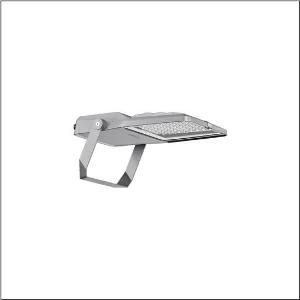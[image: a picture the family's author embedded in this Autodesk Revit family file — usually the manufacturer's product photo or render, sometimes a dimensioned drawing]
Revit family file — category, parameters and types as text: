
# Revit family: floodlight_fl_21_mini___pl61_5xa7776c2c1a_8570
name_source: partatom
category: Lighting Fixtures
units: mm (PartAtom-declared; Revit-internal decimal feet)

## family parameters
Cut with Voids When Loaded = No
Host = Face
Light Source = No
Part Type = Normal
Room Calculation Point = No
Round Connector Dimension = Use Diameter
Shared = No

## types (1)
- --- (1 x LED, 11960 lm, 89 W, 3000K)
    Apparent Load = 89 VA
    CIE Flux Codes = 33 65 98 100 100
    Color Rendering = 70
    Color Temperature = 3000K
    Default Elevation = 1800 mm
    Description = Floodlight FL 21 mini, floodlight, primary light control with lens, of PMMA, primary optical cover: protective disc, of toughened safety glass, transparent, light distribution: PL61, light emission: direct distribution, installation type: surface-mounted, LED, High Power LED, rated luminous flux: 11.960lm, luminous efficacy: 134lm/W, light colour: 730, colour temperature: 3000K, control gear: Smart Interface (Zhaga), control: flexible luminous flux parameterisation, time-dependent luminous flux control, constant luminous flux control, overheat protection, pre-setting: logarithmic dimming characteristic, with terminal, 6-pole, mains connection: 220..240V, AC, 50/60Hz, start of lifetime: 89W, end of service life: 94W, reduction: 43W, luminaire housing, of diecast aluminium, powder-coated, SITECO metallic grey (DB 702S), corrosivity category C5 mid according to DIN EN ISO 12944, suitable for swimming pools, chlorine-resistant, sealing non-destructively replaceable, mounting bracket, of steel, galvanised, powder-coated, SITECO metallic grey (DB 702S), Smart Interface below and above, protection rating (complete): IP66, insulation class (complete): insulation class II (safety insulation), certification: CE, ENEC, VDE, protection symbol: D, impact resistance: IK08, permissible operating ambient temperature: -40..+40°C, permissible operating ambient temperature for outdoor applications: -40..+50°C, standard: DIN EN 12944, LABS conformity tested according to VDMA 24364:2018-05, packaging unit: 1 piece

Light Distribution: PL61
    Height = 70 mm
    Lamp = 1 x LED
    Lamp Light Flux = 11960 lm
    Lamp Power = 89 W
    Lamp count = 1
    Length = 485 mm
    Luminous efficacy = 134 lm/W
    Manufacturer = Siteco
    ModVariant = No
    Model = 5XA7776C2C1A
    Mounting Place = Pole
    Mounting Type = Pole annexe
    Number of Poles = 1
    OnlyDefault = Yes
    Power Factor = 1
    Product Name = Floodlight FL 21 mini | PL61
    Product group = floodlight | pylon annexe
    ProductGroupID = 6201
    Protection Class = Protection class II
    Protection Degree = IP 66
    RLX_Detail_Level = 1
    RLX_Emergency_Light_Flux = 0 lm
    RLX_Emergency_Type = 0
    RLX_Emergency_Type_DB = No
    RlxData = <blob elided: 96061 chars, md5=b757be94>
    Socket = socket
    Standby Power = 0 W
    System Light Flux = 11960 lm
    System Power = 89 W
    Type Comments = factory setting: luminous flux: 100 % | dim-lin: 254 | 456 mA
    Type Image = l_1006845.jpg
    URL = http://relux.com
    VarID = @adj_173065
    Voltage = 0 V
    Weight = 0.00 kg
    Width = 337 mm

## geometry (parser evidence)
native form markers: Blend x4, Sweep x13
no freeform markers — native parametric forms only
